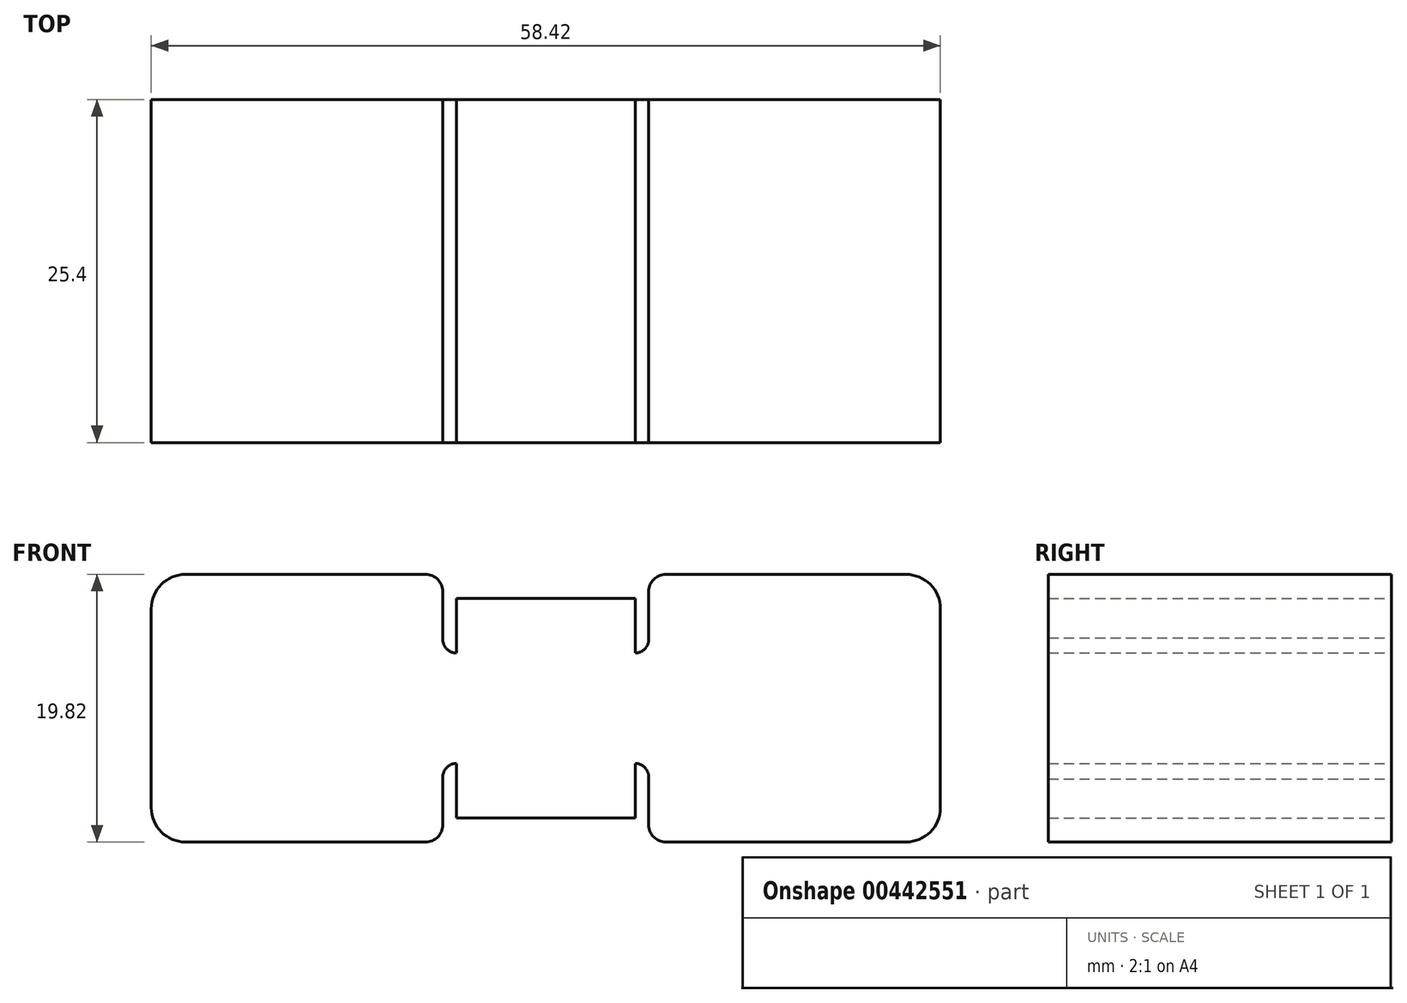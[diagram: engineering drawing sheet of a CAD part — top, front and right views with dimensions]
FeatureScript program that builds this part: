
annotation { "Feature Type Name" : "Feature", "Feature Type Description" : "" }
export const myFeature = defineFeature(function(context is Context, id is Id, definition is map)
    precondition{}
    {
        {
            var Q0;
            Q0=qCreatedBy(makeId("Front.planeOp"),FACE);
            var sketch = newSketch(context, id + "F0", { "sketchPlane" : qUnion([Q0])});
            skLineSegment(sketch, "E0", {"start": v(-17.58, 0) * mm, "end": v(-17.58, 7.37) * mm});
            skLineSegment(sketch, "E1", {"start": v(-15.04, 9.9) * mm, "end": v(2.74, 9.9) * mm});
            skLineSegment(sketch, "E2", {"start": v(4.01, 8.64) * mm, "end": v(4.01, 5.22) * mm});
            skLineSegment(sketch, "E3", {"start": v(5.02, 4.09) * mm, "end": v(5.02, 8.13) * mm});
            skLineSegment(sketch, "E4", {"start": v(5.02, 8.13) * mm, "end": v(11.63, 8.13) * mm});
            skPoint(sketch, "E5.visualSharp", {"position": v(-17.58, 9.9) * mm});
            skArc(sketch, "E5.filletArc", {"start": v(-15.04, 9.9) * mm, "mid": v(-16.83, 9.16) * mm, "end": v(-17.58, 7.37) * mm});
            skPoint(sketch, "E6.visualSharp", {"position": v(4.01, 9.9) * mm});
            skArc(sketch, "E6.filletArc", {"start": v(4.01, 8.64) * mm, "mid": v(3.64, 9.53) * mm, "end": v(2.74, 9.9) * mm});
            skArc(sketch, "E7", {"start": v(4.01, 5.22) * mm, "mid": v(4.26, 4.43) * mm, "end": v(5.02, 4.09) * mm});
            skLineSegment(sketch, "E8.MirrorCS", {"start": v(18.24, 8.13) * mm, "end": v(11.63, 8.13) * mm});
            skLineSegment(sketch, "E9.MirrorCS", {"start": v(18.24, 4.09) * mm, "end": v(18.24, 8.13) * mm});
            skArc(sketch, "E10.MirrorCS", {"start": v(19.25, 5.22) * mm, "mid": v(19, 4.43) * mm, "end": v(18.24, 4.09) * mm});
            skLineSegment(sketch, "E11.MirrorCS", {"start": v(19.25, 8.64) * mm, "end": v(19.25, 5.22) * mm});
            skPoint(sketch, "E12.MirrorP", {"position": v(19.25, 9.9) * mm});
            skArc(sketch, "E13.MirrorCS", {"start": v(19.25, 8.64) * mm, "mid": v(19.62, 9.53) * mm, "end": v(20.52, 9.9) * mm});
            skLineSegment(sketch, "E14.MirrorCS", {"start": v(38.3, 9.9) * mm, "end": v(20.52, 9.9) * mm});
            skArc(sketch, "E15.MirrorCS", {"start": v(38.3, 9.9) * mm, "mid": v(40.1, 9.16) * mm, "end": v(40.84, 7.37) * mm});
            skLineSegment(sketch, "E16.MirrorCS", {"start": v(40.84, 0) * mm, "end": v(40.84, 7.37) * mm});
            skLineSegment(sketch, "E17.MirrorCS", {"start": v(-17.58, 0) * mm, "end": v(-17.58, -7.37) * mm});
            skLineSegment(sketch, "E18.MirrorCS", {"start": v(-15.04, -9.9) * mm, "end": v(2.74, -9.9) * mm});
            skPoint(sketch, "E19.MirrorP", {"position": v(-17.58, -9.9) * mm});
            skArc(sketch, "E20.MirrorCS", {"start": v(-15.04, -9.9) * mm, "mid": v(-16.83, -9.16) * mm, "end": v(-17.58, -7.37) * mm});
            skArc(sketch, "E21.MirrorCS", {"start": v(4.01, -8.64) * mm, "mid": v(3.64, -9.53) * mm, "end": v(2.74, -9.9) * mm});
            skLineSegment(sketch, "E22.MirrorCS", {"start": v(4.01, -8.64) * mm, "end": v(4.01, -5.22) * mm});
            skArc(sketch, "E23.MirrorCS", {"start": v(4.01, -5.22) * mm, "mid": v(4.26, -4.43) * mm, "end": v(5.02, -4.09) * mm});
            skLineSegment(sketch, "E24.MirrorCS", {"start": v(5.02, -4.09) * mm, "end": v(5.02, -8.13) * mm});
            skLineSegment(sketch, "E25.MirrorCS", {"start": v(5.02, -8.13) * mm, "end": v(11.63, -8.13) * mm});
            skLineSegment(sketch, "E26.MirrorCS", {"start": v(18.24, -8.13) * mm, "end": v(11.63, -8.13) * mm});
            skLineSegment(sketch, "E27.MirrorCS", {"start": v(18.24, -4.09) * mm, "end": v(18.24, -8.13) * mm});
            skArc(sketch, "E28.MirrorCS", {"start": v(19.25, -5.22) * mm, "mid": v(19, -4.43) * mm, "end": v(18.24, -4.09) * mm});
            skLineSegment(sketch, "E29.MirrorCS", {"start": v(19.25, -8.64) * mm, "end": v(19.25, -5.22) * mm});
            skArc(sketch, "E30.MirrorCS", {"start": v(19.25, -8.64) * mm, "mid": v(19.62, -9.53) * mm, "end": v(20.52, -9.9) * mm});
            skLineSegment(sketch, "E31.MirrorCS", {"start": v(38.3, -9.9) * mm, "end": v(20.52, -9.9) * mm});
            skLineSegment(sketch, "E32.MirrorCS", {"start": v(40.84, 0) * mm, "end": v(40.84, -7.37) * mm});
            skArc(sketch, "E33.MirrorCS", {"start": v(38.3, -9.9) * mm, "mid": v(40.1, -9.16) * mm, "end": v(40.84, -7.37) * mm});
            skSolve(sketch);
        }
        {
            var Q0;
            Q0=makeQuery(id+"F0.imprint","IMPRINT",FACE,{"disambiguationData":[TD([[makeQuery(id+"F0.imprint","IMPRINT",EDGE,{"derivedFrom":sQuery(id+"F0.wireOp",EDGE,"E0")}),-1.0]])]});
            extrude(context, id + "F1", {"entities" : qUnion([Q0]), "depth" : 25.4 * mm});
        }
    });
